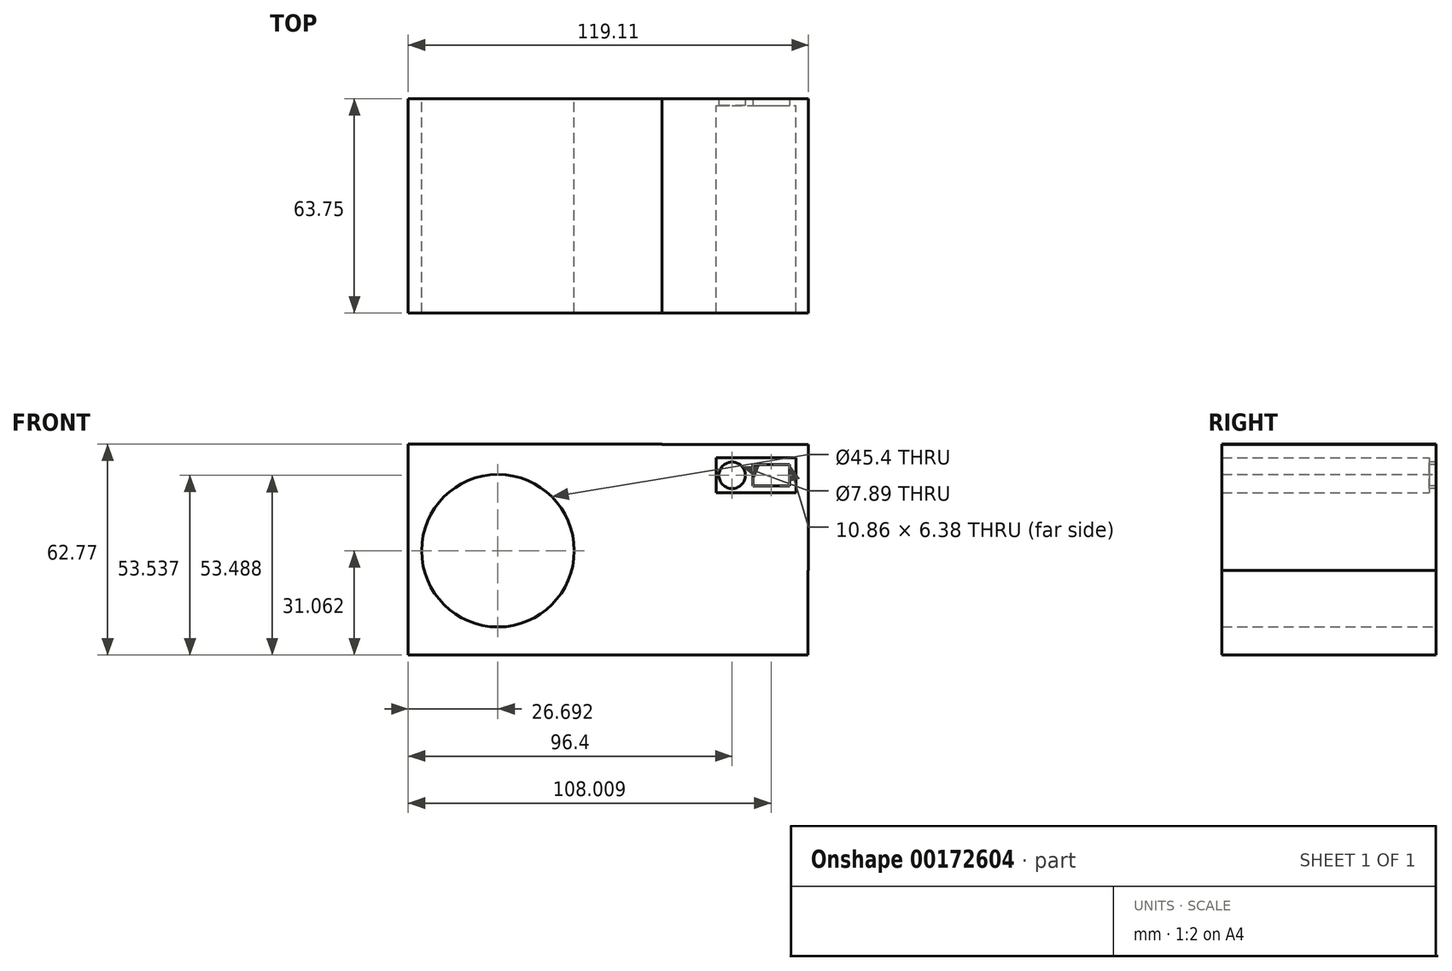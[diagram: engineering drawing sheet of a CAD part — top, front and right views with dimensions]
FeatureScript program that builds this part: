
annotation { "Feature Type Name" : "Feature", "Feature Type Description" : "" }
export const myFeature = defineFeature(function(context is Context, id is Id, definition is map)
    precondition{}
    {
        {
            var Q0;
            Q0=qCreatedBy(makeId("Front.planeOp"),FACE);
            var sketch = newSketch(context, id + "F0", { "sketchPlane" : qUnion([Q0])});
            skLineSegment(sketch, "E0", {"start": v(-93.7, 0) * mm, "end": v(0, 0) * mm});
            skLineSegment(sketch, "E1.bottom", {"start": v(0, 37.54) * mm, "end": v(43.56, 37.54) * mm});
            skLineSegment(sketch, "E1.top", {"start": v(0, 0) * mm, "end": v(43.56, 0) * mm});
            skLineSegment(sketch, "E1.left", {"start": v(43.56, 37.54) * mm, "end": v(43.56, 0) * mm});
            skLineSegment(sketch, "E1.right", {"start": v(0, 37.54) * mm, "end": v(0, 0) * mm});
            skLineSegment(sketch, "E2.bottom", {"start": v(0, 0) * mm, "end": v(-75.55, 0) * mm});
            skLineSegment(sketch, "E2.top", {"start": v(0, 37.6) * mm, "end": v(-75.55, 37.6) * mm});
            skLineSegment(sketch, "E2.left", {"start": v(0, 0) * mm, "end": v(0, 37.6) * mm});
            skLineSegment(sketch, "E2.right", {"start": v(-75.55, 0) * mm, "end": v(-75.55, 37.6) * mm});
            skLineSegment(sketch, "E3.top", {"start": v(0, -25.17) * mm, "end": v(-75.55, -25.17) * mm});
            skLineSegment(sketch, "E3.left", {"start": v(0, 0) * mm, "end": v(0, -25.17) * mm});
            skLineSegment(sketch, "E3.right", {"start": v(-75.55, 0) * mm, "end": v(-75.55, -25.17) * mm});
            skLineSegment(sketch, "E4.bottom", {"start": v(0, 0) * mm, "end": v(43.48, 0) * mm});
            skLineSegment(sketch, "E4.top", {"start": v(0, -25.17) * mm, "end": v(43.48, -25.17) * mm});
            skLineSegment(sketch, "E4.right", {"start": v(43.48, 0) * mm, "end": v(43.48, -25.17) * mm});
            skCircle(sketch, "E5", {"center": v(-48.86, 5.9) * mm, "radius": 22.7 * mm});
            skCircle(sketch, "E6", {"center": v(-48.86, 5.9) * mm, "radius": 20.25 * mm});
            skCircle(sketch, "E7", {"center": v(-48.86, 5.9) * mm, "radius": 16.96 * mm});
            skCircle(sketch, "E8", {"center": v(-48.86, 5.9) * mm, "radius": 10.4 * mm});
            skLineSegment(sketch, "E9.bottom", {"start": v(16.17, 33.55) * mm, "end": v(39.88, 33.55) * mm});
            skLineSegment(sketch, "E9.top", {"start": v(16.17, 23.09) * mm, "end": v(39.88, 23.09) * mm});
            skLineSegment(sketch, "E9.left", {"start": v(16.17, 33.55) * mm, "end": v(16.17, 23.09) * mm});
            skLineSegment(sketch, "E9.right", {"start": v(39.88, 33.55) * mm, "end": v(39.88, 23.09) * mm});
            skCircle(sketch, "E10", {"center": v(20.85, 28.32) * mm, "radius": 3.95 * mm});
            skPoint(sketch, "E10.centerSnap0", {"position": v(16.17, 28.32) * mm});
            skLineSegment(sketch, "E11.bottom", {"start": v(27.03, 31.56) * mm, "end": v(37.89, 31.56) * mm});
            skLineSegment(sketch, "E11.top", {"start": v(27.03, 25.18) * mm, "end": v(37.89, 25.18) * mm});
            skLineSegment(sketch, "E11.left", {"start": v(27.03, 31.56) * mm, "end": v(27.03, 25.18) * mm});
            skLineSegment(sketch, "E11.right", {"start": v(37.89, 31.56) * mm, "end": v(37.89, 25.18) * mm});
            skSolve(sketch);
        }
        {
            var Q0;
            Q0 = qSketchRegion(id + "F0", true);
            var Q1;
            {var subQ0=sQuery(id+"F0.wireOp",EDGE,"E7");var subQ1=sQuery(id+"F0.wireOp",EDGE,"E2.bottom");var subQ2=makeQuery(id+"F0.imprint","INTERSECT",VERTEX,{"disambiguationData":[OD(0.0)],"derivedFrom":[subQ1,subQ0]});Q1=makeQuery(id+"F0.imprint","IMPRINT",FACE,{"disambiguationData":[TD([[makeQuery(id+"F0.imprint","IMPRINT",EDGE,{"disambiguationData":[TD([[subQ2,-1.0]])],"derivedFrom":subQ1}),1.0]])]});}
            var Q2;
            {var subQ0=sQuery(id+"F0.wireOp",EDGE,"E6");var subQ1=sQuery(id+"F0.wireOp",EDGE,"E2.bottom");var subQ2=makeQuery(id+"F0.imprint","INTERSECT",VERTEX,{"disambiguationData":[OD(0.0)],"derivedFrom":[subQ1,subQ0]});Q2=makeQuery(id+"F0.imprint","IMPRINT",FACE,{"disambiguationData":[TD([[makeQuery(id+"F0.imprint","IMPRINT",EDGE,{"disambiguationData":[TD([[subQ2,-1.0]])],"derivedFrom":subQ1}),-1.0]])]});}
            var Q3;
            {var subQ0=sQuery(id+"F0.wireOp",EDGE,"E5");var subQ1=sQuery(id+"F0.wireOp",EDGE,"E2.bottom");var subQ2=makeQuery(id+"F0.imprint","INTERSECT",VERTEX,{"disambiguationData":[OD(0.0)],"derivedFrom":[subQ1,subQ0]});Q3=makeQuery(id+"F0.imprint","IMPRINT",FACE,{"disambiguationData":[TD([[makeQuery(id+"F0.imprint","IMPRINT",EDGE,{"disambiguationData":[TD([[subQ2,-1.0]])],"derivedFrom":subQ1}),1.0]])]});}
            var Q4;
            {var subQ0=sQuery(id+"F0.wireOp",EDGE,"E8");var subQ1=sQuery(id+"F0.wireOp",EDGE,"E2.bottom");var subQ2=makeQuery(id+"F0.imprint","INTERSECT",VERTEX,{"disambiguationData":[OD(0.0)],"derivedFrom":[subQ1,subQ0]});Q4=makeQuery(id+"F0.imprint","IMPRINT",FACE,{"disambiguationData":[TD([[makeQuery(id+"F0.imprint","IMPRINT",EDGE,{"disambiguationData":[TD([[subQ2,-1.0]])],"derivedFrom":subQ1}),-1.0]])]});}
            extrude(context, id + "F1", {"entities" : qUnion([Q0, Q1, Q2, Q3, Q4]), "depth" : 25.4 * mm});
        }
        {
            var Q0;
            Q0 = qSketchRegion(id + "F0", true);
            var Q1;
            {var subQ0=sQuery(id+"F0.wireOp",EDGE,"E8");var subQ1=sQuery(id+"F0.wireOp",EDGE,"E2.bottom");var subQ2=makeQuery(id+"F0.imprint","INTERSECT",VERTEX,{"disambiguationData":[OD(0.0)],"derivedFrom":[subQ1,subQ0]});Q1=makeQuery(id+"F0.imprint","IMPRINT",FACE,{"disambiguationData":[TD([[makeQuery(id+"F0.imprint","IMPRINT",EDGE,{"disambiguationData":[TD([[subQ2,-1.0]])],"derivedFrom":subQ1}),1.0]])]});}
            var Q2;
            {var subQ0=sQuery(id+"F0.wireOp",EDGE,"E7");var subQ1=sQuery(id+"F0.wireOp",EDGE,"E2.bottom");var subQ2=makeQuery(id+"F0.imprint","INTERSECT",VERTEX,{"disambiguationData":[OD(0.0)],"derivedFrom":[subQ1,subQ0]});Q2=makeQuery(id+"F0.imprint","IMPRINT",FACE,{"disambiguationData":[TD([[makeQuery(id+"F0.imprint","IMPRINT",EDGE,{"disambiguationData":[TD([[subQ2,-1.0]])],"derivedFrom":subQ1}),-1.0]])]});}
            var Q3;
            {var subQ0=sQuery(id+"F0.wireOp",EDGE,"E6");var subQ1=sQuery(id+"F0.wireOp",EDGE,"E2.bottom");var subQ2=makeQuery(id+"F0.imprint","INTERSECT",VERTEX,{"disambiguationData":[OD(0.0)],"derivedFrom":[subQ1,subQ0]});Q3=makeQuery(id+"F0.imprint","IMPRINT",FACE,{"disambiguationData":[TD([[makeQuery(id+"F0.imprint","IMPRINT",EDGE,{"disambiguationData":[TD([[subQ2,-1.0]])],"derivedFrom":subQ1}),1.0]])]});}
            var Q4;
            {var subQ0=sQuery(id+"F0.wireOp",EDGE,"E5");var subQ1=sQuery(id+"F0.wireOp",EDGE,"E2.bottom");var subQ2=makeQuery(id+"F0.imprint","INTERSECT",VERTEX,{"disambiguationData":[OD(0.0)],"derivedFrom":[subQ1,subQ0]});Q4=makeQuery(id+"F0.imprint","IMPRINT",FACE,{"disambiguationData":[TD([[makeQuery(id+"F0.imprint","IMPRINT",EDGE,{"disambiguationData":[TD([[subQ2,-1.0]])],"derivedFrom":subQ1}),-1.0]])]});}
            extrude(context, id + "F2", {"entities" : qUnion([Q0, Q1, Q2, Q3, Q4]), "operationType" : NewBodyOperationType.ADD, "depth" : 61.72 * mm});
        }
        {
            var Q0;
            Q0 = qSketchRegion(id + "F0", true);
            extrude(context, id + "F3", {"entities" : qUnion([Q0]), "operationType" : NewBodyOperationType.ADD, "depth" : 25.4 * mm});
        }
        {
            var Q0;
            Q0=makeQuery(id+"F1.opExtrude","CAP_FACE",FACE,{"disambiguationData":[OSD([sQuery(id+"F0.wireOp",EDGE,"E6"),sQuery(id+"F0.wireOp",EDGE,"E8")])],"isStart":false});
            var Q1;
            Q1=makeQuery(id+"F1.opExtrude","CAP_FACE",FACE,{"disambiguationData":[OSD([sQuery(id+"F0.wireOp",EDGE,"E2.bottom"),sQuery(id+"F0.wireOp",EDGE,"E7"),sQuery(id+"F0.wireOp",EDGE,"E8")])],"isStart":false});
            var Q2;
            Q2 = qSketchRegion(id + "F0", true);
            var Q3;
            Q3=makeQuery(id+"F0.imprint","IMPRINT",FACE,{"disambiguationData":[TD([[makeQuery(id+"F0.imprint","IMPRINT",EDGE,{"derivedFrom":sQuery(id+"F0.wireOp",EDGE,"E9.bottom")}),-1.0]])]});
            extrude(context, id + "F4", {"entities" : qUnion([Q0, Q1, Q2, Q3]), "operationType" : NewBodyOperationType.ADD, "oppositeDirection" : true, "depth" : 2.03 * mm});
        }
    });
